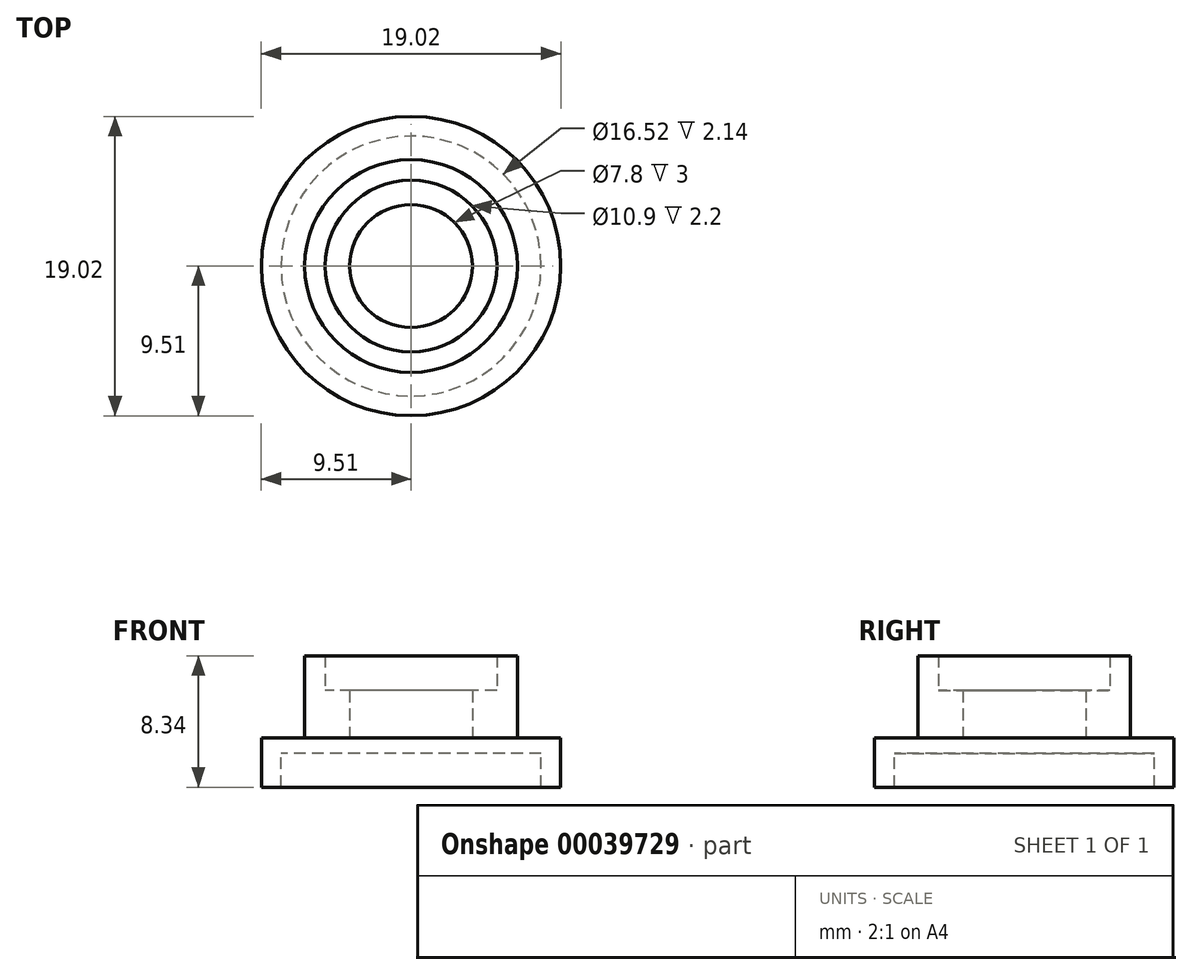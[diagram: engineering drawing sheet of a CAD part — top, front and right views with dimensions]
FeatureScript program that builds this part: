
annotation { "Feature Type Name" : "Feature", "Feature Type Description" : "" }
export const myFeature = defineFeature(function(context is Context, id is Id, definition is map)
    precondition{}
    {
        {
            var Q0;
            Q0=qCreatedBy(makeId("Top.planeOp"),FACE);
            var sketch = newSketch(context, id + "F0", { "sketchPlane" : qUnion([Q0])});
            skCircle(sketch, "E0", {"center": v(0, 0) * mm, "radius": 6.75 * mm});
            skCircle(sketch, "E1", {"center": v(0, 0) * mm, "radius": 8.26 * mm});
            skCircle(sketch, "E2", {"center": v(0, 0) * mm, "radius": 9.5 * mm});
            skCircle(sketch, "E3", {"center": v(0, 0) * mm, "radius": 3.9 * mm});
            skCircle(sketch, "E4", {"center": v(0, 0) * mm, "radius": 5.45 * mm});
            skSolve(sketch);
        }
        {
            var Q0;
            Q0=makeQuery(id+"F0.imprint","IMPRINT",FACE,{"disambiguationData":[TD([[makeQuery(id+"F0.imprint","IMPRINT",EDGE,{"derivedFrom":sQuery(id+"F0.wireOp",EDGE,"E1")}),-1.0]])]});
            extrude(context, id + "F1", {"entities" : qUnion([Q0]), "oppositeDirection" : true, "depth" : 3.14 * mm});
        }
        {
            var Q0;
            Q0=makeQuery(id+"F0.imprint","IMPRINT",FACE,{"disambiguationData":[TD([[makeQuery(id+"F0.imprint","IMPRINT",EDGE,{"derivedFrom":sQuery(id+"F0.wireOp",EDGE,"E4")}),-1.0]])]});
            extrude(context, id + "F2", {"entities" : qUnion([Q0]), "depth" : 5.2 * mm, "hasSecondDirection" : true, "secondDirectionOppositeDirection" : true, "secondDirectionDepth" : 1 * mm});
        }
        {
            var Q0;
            Q0=makeQuery(id+"F0.imprint","IMPRINT",FACE,{"disambiguationData":[TD([[makeQuery(id+"F0.imprint","IMPRINT",EDGE,{"derivedFrom":sQuery(id+"F0.wireOp",EDGE,"E3")}),-1.0]])]});
            extrude(context, id + "F3", {"entities" : qUnion([Q0]), "operationType" : NewBodyOperationType.ADD, "depth" : 3 * mm, "hasSecondDirection" : true, "secondDirectionOppositeDirection" : true, "secondDirectionDepth" : 1 * mm});
        }
        {
            var Q0;
            Q0=makeQuery(id+"F0.imprint","IMPRINT",FACE,{"disambiguationData":[TD([[makeQuery(id+"F0.imprint","IMPRINT",EDGE,{"derivedFrom":sQuery(id+"F0.wireOp",EDGE,"E1")}),1.0]])]});
            var Q1;
            Q1=makeQuery(id+"F0.imprint","IMPRINT",FACE,{"disambiguationData":[TD([[makeQuery(id+"F0.imprint","IMPRINT",EDGE,{"derivedFrom":sQuery(id+"F0.wireOp",EDGE,"E3")}),1.0]])]});
            extrude(context, id + "F4", {"entities" : qUnion([Q0, Q1]), "operationType" : NewBodyOperationType.ADD, "oppositeDirection" : true, "depth" : 1 * mm});
        }
    });
